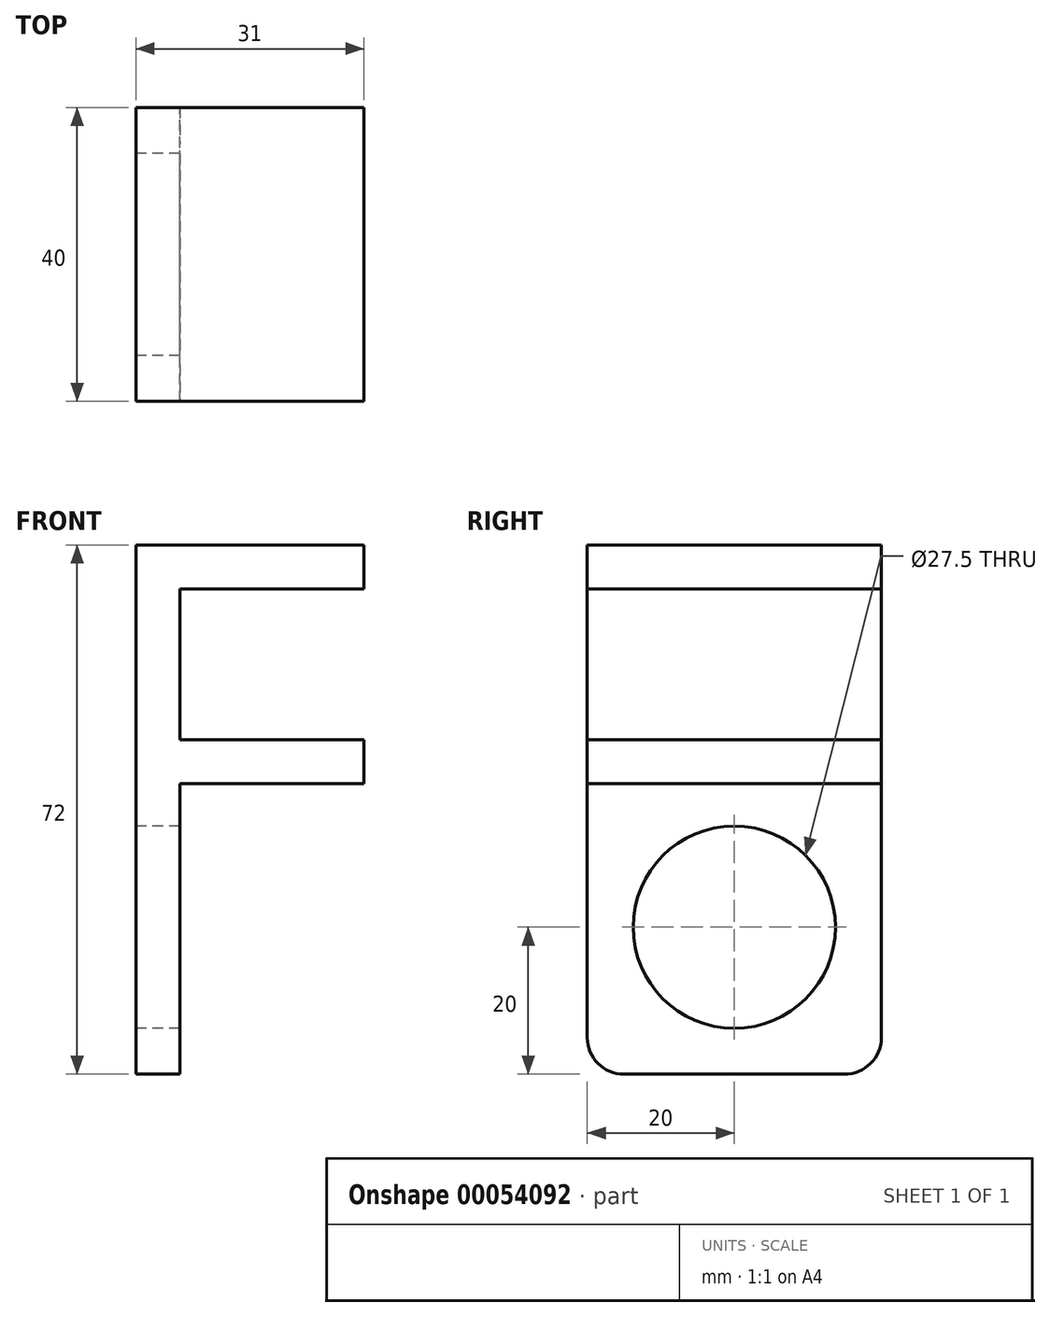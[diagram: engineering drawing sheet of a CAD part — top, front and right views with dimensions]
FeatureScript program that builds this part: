
annotation { "Feature Type Name" : "Feature", "Feature Type Description" : "" }
export const myFeature = defineFeature(function(context is Context, id is Id, definition is map)
    precondition{}
    {
        {
            var Q0;
            Q0=qCreatedBy(makeId("Front.planeOp"),FACE);
            var sketch = newSketch(context, id + "F0", { "sketchPlane" : qUnion([Q0])});
            skLineSegment(sketch, "E0.bottom", {"start": v(0, 0) * mm, "end": v(6, 0) * mm});
            skLineSegment(sketch, "E0.top", {"start": v(0, 72) * mm, "end": v(6, 72) * mm});
            skLineSegment(sketch, "E0.left", {"start": v(0, 0) * mm, "end": v(0, 72) * mm});
            skLineSegment(sketch, "E0.right", {"start": v(6, 0) * mm, "end": v(6, 72) * mm});
            skLineSegment(sketch, "E1.bottom", {"start": v(6, 72) * mm, "end": v(31, 72) * mm});
            skLineSegment(sketch, "E1.top", {"start": v(6, 66) * mm, "end": v(31, 66) * mm});
            skLineSegment(sketch, "E1.left", {"start": v(6, 72) * mm, "end": v(6, 66) * mm});
            skLineSegment(sketch, "E2.right", {"start": v(31, 72) * mm, "end": v(31, 66) * mm});
            skLineSegment(sketch, "E3.bottom", {"start": v(6, 45.5) * mm, "end": v(31, 45.5) * mm});
            skLineSegment(sketch, "E3.top", {"start": v(6, 39.5) * mm, "end": v(31, 39.5) * mm});
            skLineSegment(sketch, "E3.left", {"start": v(6, 45.5) * mm, "end": v(6, 39.5) * mm});
            skLineSegment(sketch, "E3.right", {"start": v(31, 45.5) * mm, "end": v(31, 39.5) * mm});
            skSolve(sketch);
        }
        {
            var Q0;
            Q0=qSketchRegion(id+"F0",true);
            extrude(context, id + "F1", {"entities" : qUnion([Q0]), "depth" : 40 * mm});
        }
        {
            var Q0;
            Q0=makeQuery(id+"F1.opExtrude","CAP_EDGE",EDGE,{"disambiguationData":[OSD([sQuery(id+"F0.wireOp",EDGE,"E0.bottom")])],"isStart":true});
            var Q1;
            Q1=makeQuery(id+"F1.opExtrude","CAP_EDGE",EDGE,{"disambiguationData":[OSD([sQuery(id+"F0.wireOp",EDGE,"E0.bottom")])],"isStart":false});
            fillet(context, id + "F2", {"entities" : qUnion([Q0, Q1]), "radius" : 5 * mm, "tangentPropagation" : true, "allowEdgeOverflow" : false});
        }
        {
            var Q0;
            Q0=makeQuery(id+"F1.opExtrude","SWEPT_FACE",FACE,{"disambiguationData":[OSD([sQuery(id+"F0.wireOp",EDGE,"E0.left")])]});
            var sketch = newSketch(context, id + "F3", { "sketchPlane" : qUnion([Q0])});
            skCircle(sketch, "E4", {"center": v(20, 20) * mm, "radius": 13.75 * mm});
            skSolve(sketch);
        }
        {
            var Q0;
            Q0=qSketchRegion(id+"F3",true);
            extrude(context, id + "F4", {"entities" : qUnion([Q0]), "operationType" : NewBodyOperationType.REMOVE, "oppositeDirection" : true, "depth" : 25 * mm});
        }
    });
